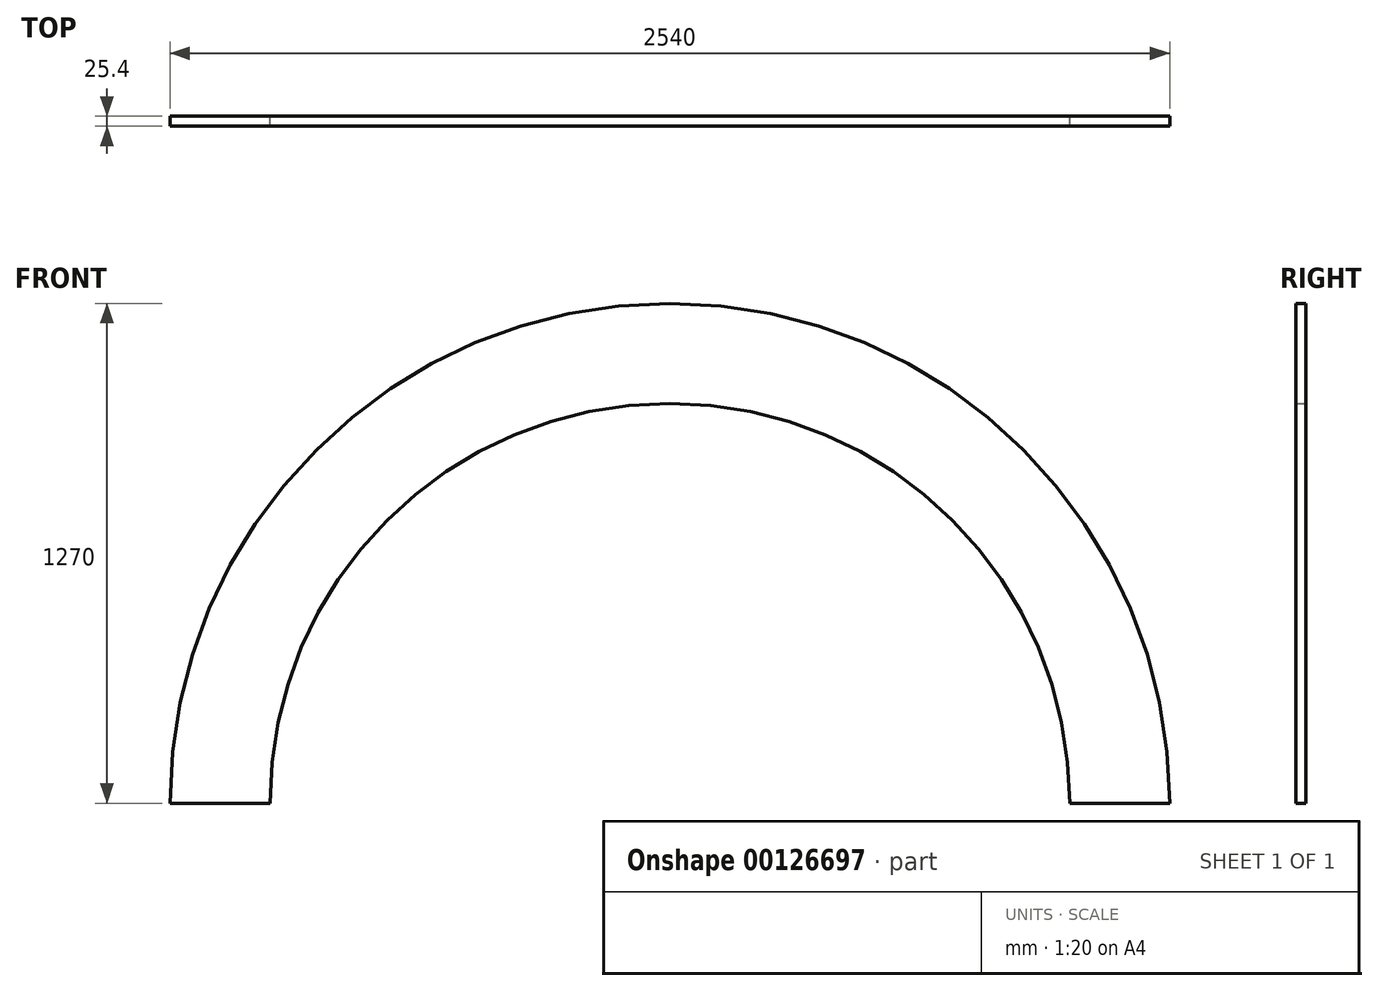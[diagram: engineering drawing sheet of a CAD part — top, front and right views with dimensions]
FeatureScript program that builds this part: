
annotation { "Feature Type Name" : "Feature", "Feature Type Description" : "" }
export const myFeature = defineFeature(function(context is Context, id is Id, definition is map)
    precondition{}
    {
        {
            var Q0;
            Q0=qCreatedBy(makeId("Front.planeOp"),FACE);
            var sketch = newSketch(context, id + "F0", { "sketchPlane" : qUnion([Q0])});
            skLineSegment(sketch, "E0", {"start": v(-1270, 0) * mm, "end": v(0, 0) * mm});
            skLineSegment(sketch, "E1", {"start": v(0, 0) * mm, "end": v(1270, 0) * mm});
            skArc(sketch, "E2", {"start": v(1270, 0) * mm, "mid": v(0, 1270) * mm, "end": v(-1270, 0) * mm});
            skArc(sketch, "E3", {"start": v(1016, 0) * mm, "mid": v(0, 1016) * mm, "end": v(-1016, 0) * mm});
            skSolve(sketch);
        }
        {
            var Q0;
            {var subQ0=sQuery(id+"F0.wireOp",EDGE,"E2");Q0=makeQuery(id+"F0.imprint","IMPRINT",FACE,{"disambiguationData":[TD([[makeQuery(id+"F0.imprint","IMPRINT",EDGE,{"derivedFrom":subQ0}),1.0]])]});}
            extrude(context, id + "F1", {"entities" : qUnion([Q0]), "depth" : 25.4 * mm});
        }
    });
